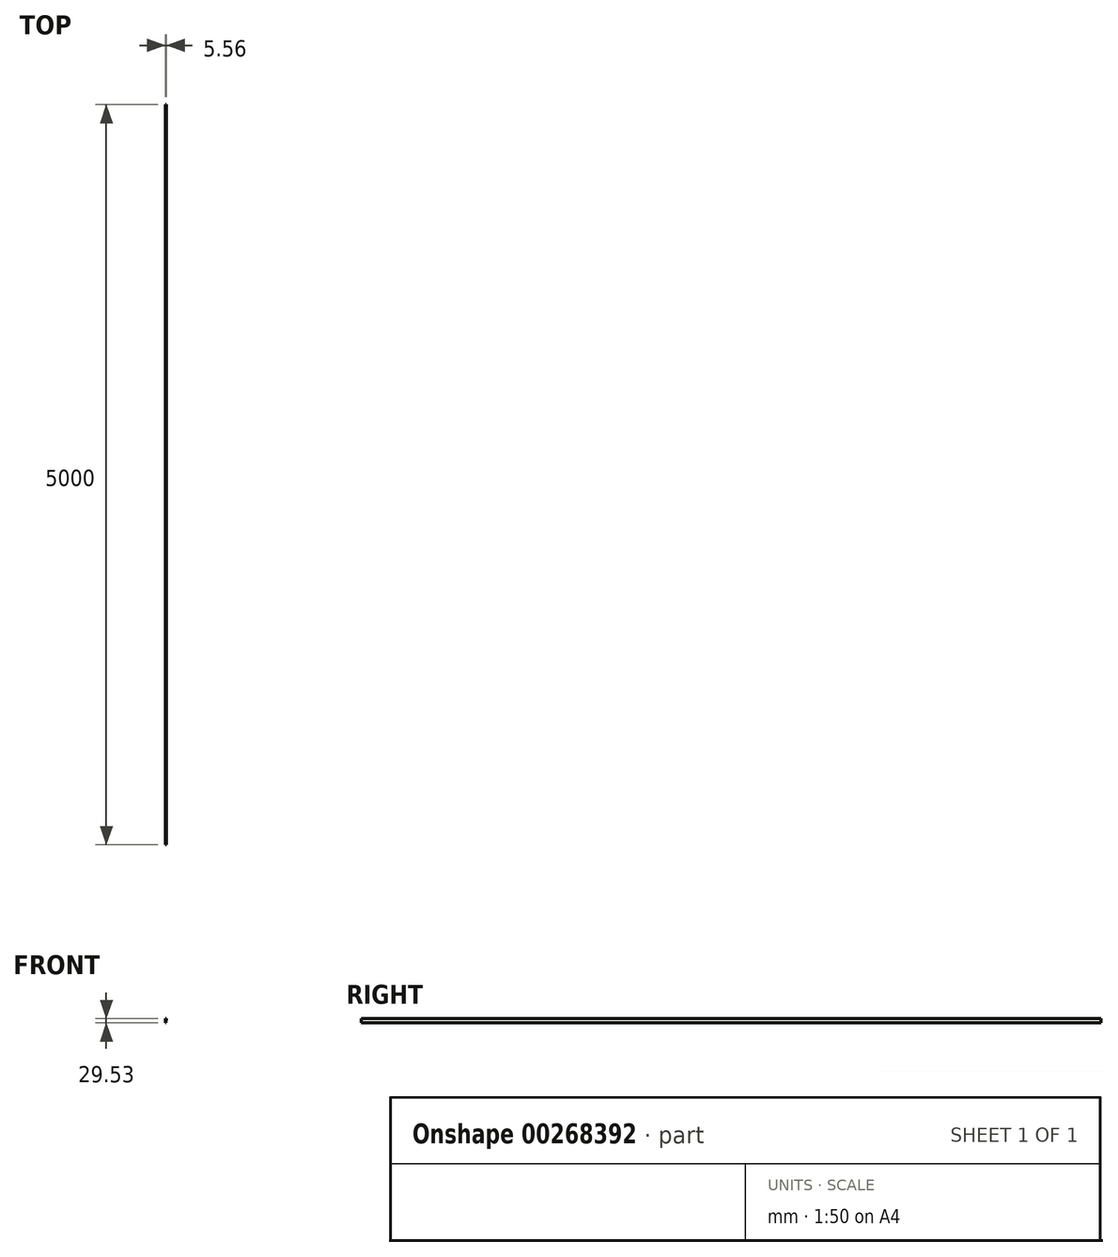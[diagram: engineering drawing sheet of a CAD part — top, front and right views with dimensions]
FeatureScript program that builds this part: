
annotation { "Feature Type Name" : "Feature", "Feature Type Description" : "" }
export const myFeature = defineFeature(function(context is Context, id is Id, definition is map)
    precondition{}
    {
        {
            var Q0;
            Q0=qCreatedBy(makeId("Front.planeOp"),FACE);
            var sketch = newSketch(context, id + "F0", { "sketchPlane" : qUnion([Q0])});
            skCircle(sketch, "E0", {"center": v(0, 0) * mm, "radius": 32 * mm});
            skLineSegment(sketch, "E1", {"start": v(0, 0) * mm, "end": v(-0.71, 32) * mm});
            skLineSegment(sketch, "E2", {"start": v(0, 0) * mm, "end": v(4.85, 31.63) * mm});
            skSolve(sketch);
        }
        {
            var Q0;
            {var subQ0=sQuery(id+"F0.wireOp",EDGE,"E1");Q0=makeQuery(id+"F0.imprint","IMPRINT",FACE,{"disambiguationData":[TD([[makeQuery(id+"F0.imprint","IMPRINT",EDGE,{"derivedFrom":subQ0}),-1.0]])]});}
            extrude(context, id + "F1", {"entities" : qUnion([Q0]), "depth" : 5000 * mm, "offsetDistance" : 25 * mm});
        }
        {
            var Q0;
            Q0=makeQuery(id+"F1.opExtrude","CAP_FACE",FACE,{"disambiguationData":[OSD([sQuery(id+"F0.wireOp",EDGE,"E0"),sQuery(id+"F0.wireOp",EDGE,"E1"),sQuery(id+"F0.wireOp",EDGE,"E2")])],"isStart":false});
            var sketch = newSketch(context, id + "F2", { "sketchPlane" : qUnion([Q0])});
            skCircle(sketch, "E3", {"center": v(0, 0) * mm, "radius": 2.5 * mm});
            skSolve(sketch);
        }
        {
            var Q0;
            {var subQ0=sQuery(id+"F2.wireOp",EDGE,"E3");var subQ1=makeQuery(id+"F1.opExtrude","CAP_EDGE",EDGE,{"disambiguationData":[OSD([sQuery(id+"F0.wireOp",EDGE,"E1")])],"isStart":false});var subQ2=makeQuery(id+"F2.imprint","INTERSECT",VERTEX,{"derivedFrom":[subQ1,subQ0]});Q0=makeQuery(id+"F2.imprint","IMPRINT",FACE,{"disambiguationData":[TD([[makeQuery(id+"F2.imprint","IMPRINT",EDGE,{"disambiguationData":[TD([[subQ2,1.0]])],"derivedFrom":subQ0}),1.0]])]});}
            extrude(context, id + "F3", {"entities" : qUnion([Q0]), "operationType" : NewBodyOperationType.REMOVE, "endBound" : BoundingType.THROUGH_ALL, "oppositeDirection" : true, "depth" : 25 * mm, "offsetDistance" : 25 * mm});
        }
    });
